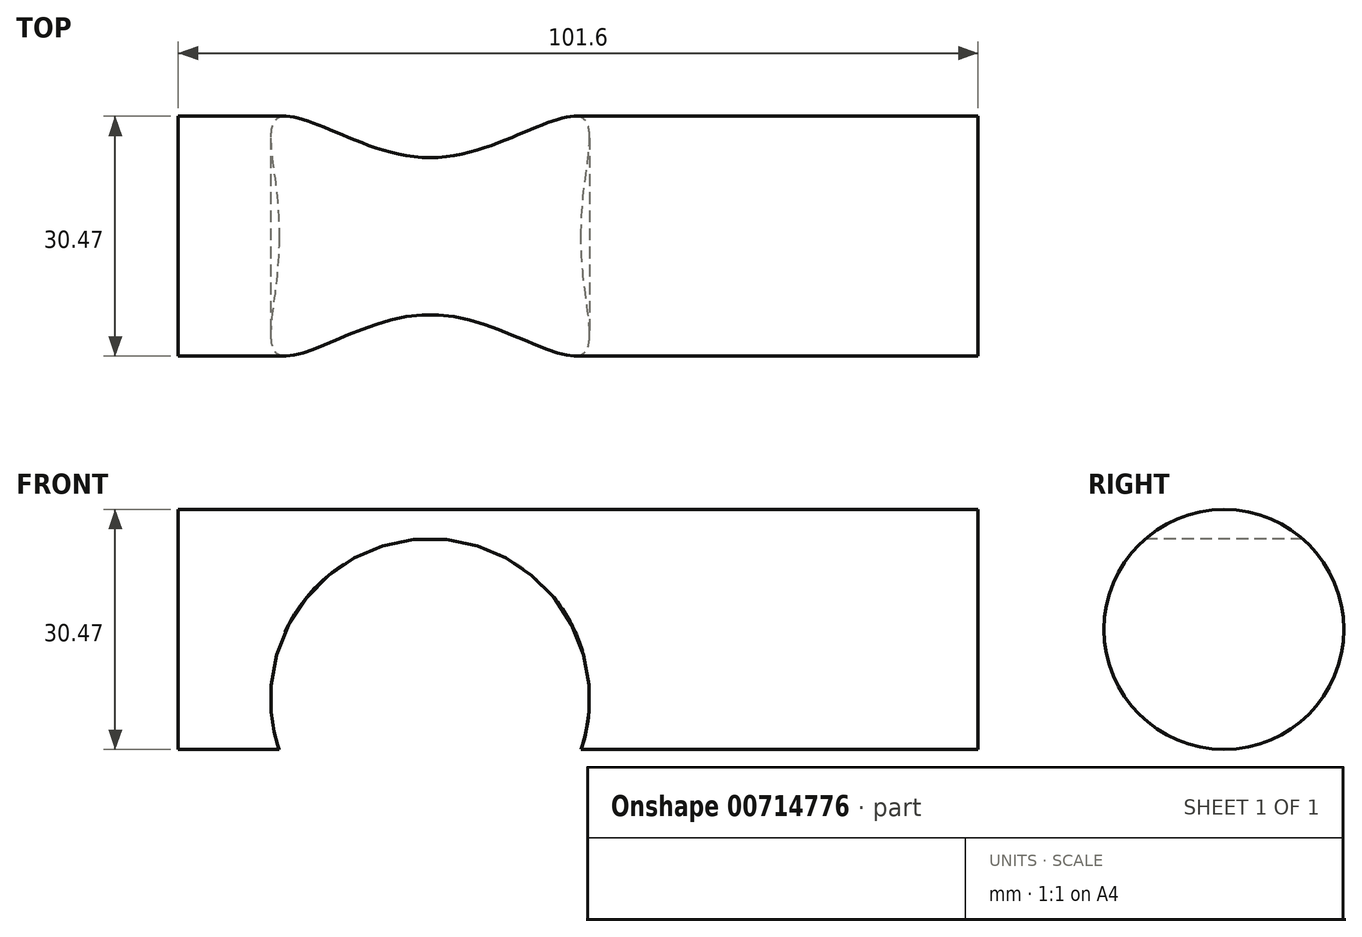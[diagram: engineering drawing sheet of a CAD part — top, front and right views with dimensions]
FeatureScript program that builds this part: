
annotation { "Feature Type Name" : "Feature", "Feature Type Description" : "" }
export const myFeature = defineFeature(function(context is Context, id is Id, definition is map)
    precondition{}
    {
        {
            var Q0;
            Q0=qCreatedBy(makeId("Front.planeOp"),FACE);
            var sketch = newSketch(context, id + "F0", { "sketchPlane" : qUnion([Q0])});
            skLineSegment(sketch, "E0.bottom", {"start": v(-55.53, 53.45) * mm, "end": v(46.07, 53.45) * mm});
            skLineSegment(sketch, "E0.top", {"start": v(-55.53, -48.15) * mm, "end": v(46.07, -48.15) * mm});
            skLineSegment(sketch, "E0.left", {"start": v(-55.53, 53.45) * mm, "end": v(-55.53, -48.15) * mm});
            skLineSegment(sketch, "E0.right", {"start": v(46.07, 53.45) * mm, "end": v(46.07, -48.15) * mm});
            skSolve(sketch);
        }
        {
            var Q0;
            Q0 = qSketchRegion(id + "F0", true);
            extrude(context, id + "F1", {"entities" : qUnion([Q0]), "depth" : 101.6 * mm, "offsetDistance" : 25.4 * mm});
        }
        {
            var Q0;
            Q0=makeQuery(id+"F1.opExtrude","CAP_FACE",FACE,{"disambiguationData":[OSD([sQuery(id+"F0.wireOp",EDGE,"E0.bottom"),sQuery(id+"F0.wireOp",EDGE,"E0.top"),sQuery(id+"F0.wireOp",EDGE,"E0.left"),sQuery(id+"F0.wireOp",EDGE,"E0.right")])],"isStart":false});
            var sketch = newSketch(context, id + "F2", { "sketchPlane" : qUnion([Q0])});
            skCircle(sketch, "E1", {"center": v(-23.54, 27.65) * mm, "radius": 20.26 * mm});
            skSolve(sketch);
        }
        {
            var Q0;
            Q0=makeQuery(id+"F2.imprint","IMPRINT",FACE,{"disambiguationData":[TD([[makeQuery(id+"F2.imprint","IMPRINT",EDGE,{"derivedFrom":sQuery(id+"F2.wireOp",EDGE,"E1")}),1.0]])]});
            extrude(context, id + "F3", {"entities" : qUnion([Q0]), "operationType" : NewBodyOperationType.REMOVE, "endBound" : BoundingType.THROUGH_ALL, "oppositeDirection" : true, "depth" : 101.6 * mm, "offsetDistance" : 25.4 * mm});
        }
        {
            var Q0;
            Q0=makeQuery(id+"F1.opExtrude","SWEPT_FACE",FACE,{"disambiguationData":[OSD([sQuery(id+"F0.wireOp",EDGE,"E0.left")])]});
            var sketch = newSketch(context, id + "F4", { "sketchPlane" : qUnion([Q0])});
            skCircle(sketch, "E2", {"center": v(48.24, 36.4) * mm, "radius": 15.24 * mm});
            skSolve(sketch);
        }
        {
            var Q0;
            Q0 = qSketchRegion(id + "F4", true);
            extrude(context, id + "F5", {"entities" : qUnion([Q0]), "operationType" : NewBodyOperationType.INTERSECT, "endBound" : BoundingType.THROUGH_ALL, "oppositeDirection" : true, "depth" : 101.6 * mm, "offsetDistance" : 25.4 * mm});
        }
    });
